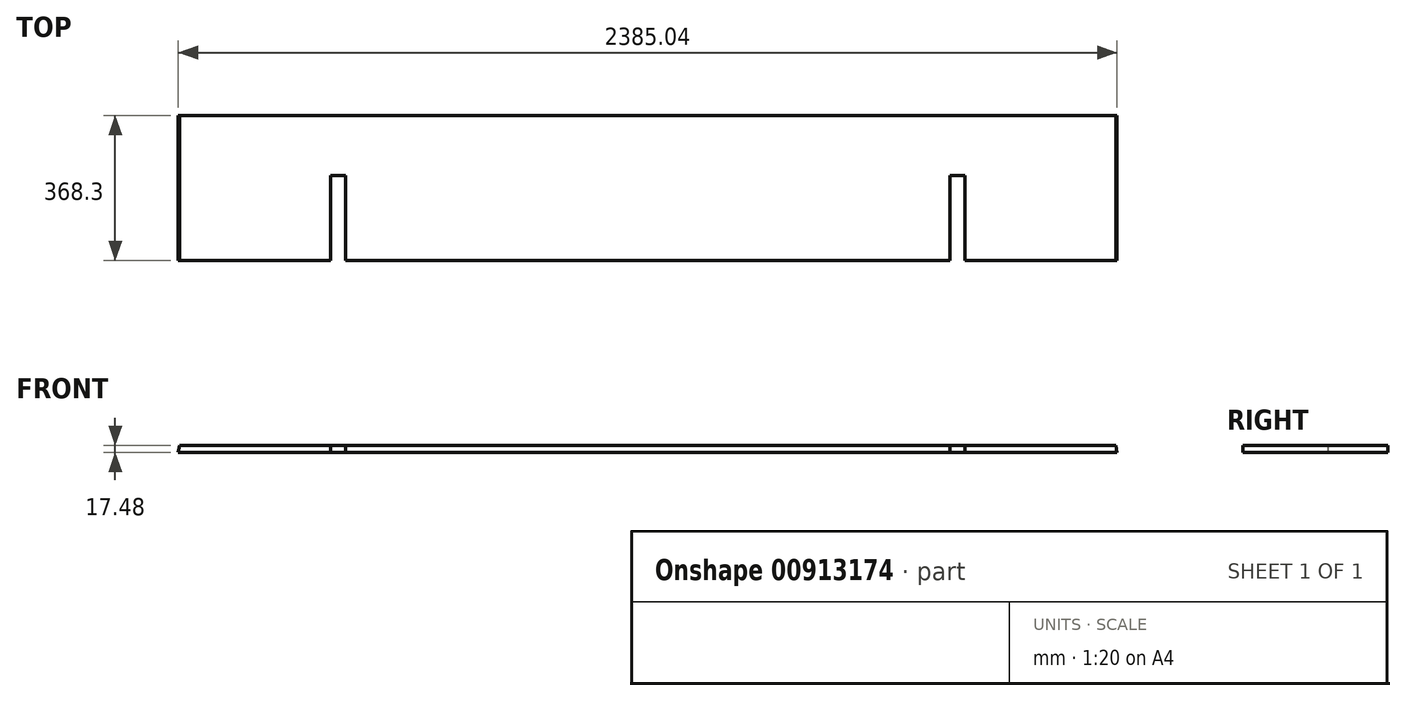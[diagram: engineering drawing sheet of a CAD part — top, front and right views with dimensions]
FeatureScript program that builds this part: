
annotation { "Feature Type Name" : "Feature", "Feature Type Description" : "" }
export const myFeature = defineFeature(function(context is Context, id is Id, definition is map)
    precondition{}
    {
        {
            var Q0;
            Q0=qCreatedBy(makeId("Front.planeOp"),FACE);
            var sketch = newSketch(context, id + "F0", { "sketchPlane" : qUnion([Q0])});
            skLineSegment(sketch, "E0.bottom", {"start": v(-1192.52, 0) * mm, "end": v(1192.52, 0) * mm});
            skLineSegment(sketch, "E0.top", {"start": v(-1189.04, 17.48) * mm, "end": v(1189.04, 17.48) * mm});
            skLineSegment(sketch, "E0.left", {"start": v(-1192.52, 0) * mm, "end": v(-1189.04, 17.48) * mm});
            skLineSegment(sketch, "E0.right", {"start": v(1192.52, 0) * mm, "end": v(1189.04, 17.48) * mm});
            skPoint(sketch, "E1", {"position": v(0, 0) * mm});
            skPoint(sketch, "E2", {"position": v(-1190.78, 8.74) * mm});
            skPoint(sketch, "E3", {"position": v(1190.78, 8.74) * mm});
            skLineSegment(sketch, "E4", {"start": v(-1190.78, 8.74) * mm, "end": v(1190.78, 8.74) * mm, "construction": true});
            skSolve(sketch);
        }
        {
            var Q0;
            Q0 = qSketchRegion(id + "F0", true);
            extrude(context, id + "F1", {"entities" : qUnion([Q0]), "depth" : 368.3 * mm, "offsetDistance" : 25.4 * mm});
        }
        {
            var Q0;
            Q0=makeQuery(id+"F1.opExtrude","SWEPT_FACE",FACE,{"disambiguationData":[OSD([sQuery(id+"F0.wireOp",EDGE,"E0.bottom")])]});
            var sketch = newSketch(context, id + "F2", { "sketchPlane" : qUnion([Q0])});
            skLineSegment(sketch, "E5.bottom", {"start": v(-805.67, 368.3) * mm, "end": v(-767.57, 368.3) * mm});
            skLineSegment(sketch, "E5.top", {"start": v(-805.67, 152.4) * mm, "end": v(-767.57, 152.4) * mm});
            skLineSegment(sketch, "E5.left", {"start": v(-805.67, 152.4) * mm, "end": v(-805.67, 368.3) * mm});
            skLineSegment(sketch, "E5.right", {"start": v(-767.57, 152.4) * mm, "end": v(-767.57, 368.3) * mm});
            skLineSegment(sketch, "E6.bottom", {"start": v(767.57, 152.4) * mm, "end": v(805.67, 152.4) * mm});
            skLineSegment(sketch, "E6.top", {"start": v(767.57, 368.3) * mm, "end": v(805.67, 368.3) * mm});
            skLineSegment(sketch, "E6.left", {"start": v(767.57, 368.3) * mm, "end": v(767.57, 152.4) * mm});
            skLineSegment(sketch, "E6.right", {"start": v(805.67, 368.3) * mm, "end": v(805.67, 152.4) * mm});
            skLineSegment(sketch, "E7", {"start": v(-1192.52, 368.3) * mm, "end": v(-805.67, 368.3) * mm});
            skLineSegment(sketch, "E8", {"start": v(805.67, 368.3) * mm, "end": v(1192.52, 368.3) * mm});
            skSolve(sketch);
        }
        {
            var Q0;
            Q0 = qSketchRegion(id + "F2", true);
            extrude(context, id + "F3", {"entities" : qUnion([Q0]), "operationType" : NewBodyOperationType.REMOVE, "endBound" : BoundingType.THROUGH_ALL, "oppositeDirection" : true, "depth" : 25.4 * mm, "offsetDistance" : 25.4 * mm});
        }
    });
